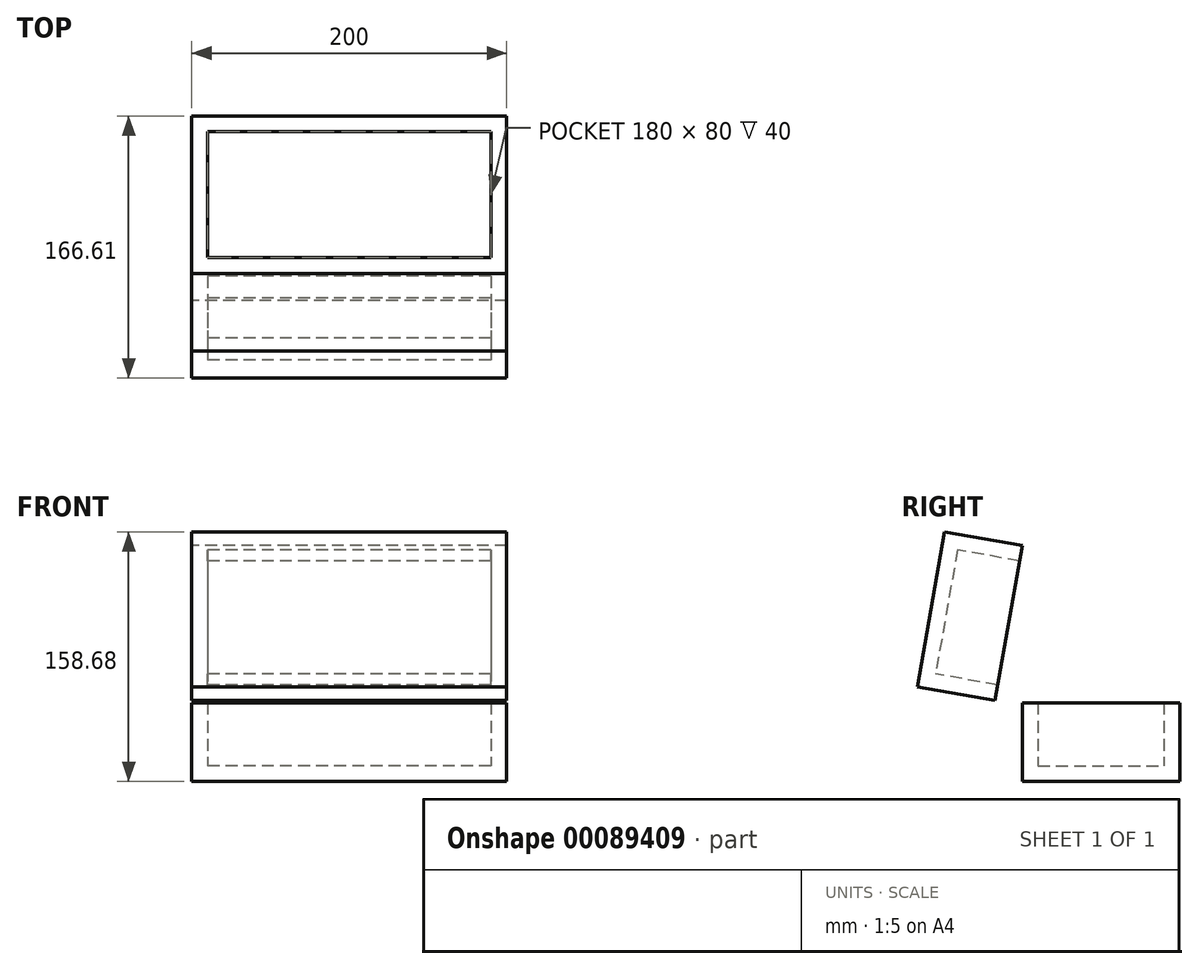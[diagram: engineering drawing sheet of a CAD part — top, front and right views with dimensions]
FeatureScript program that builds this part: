
annotation { "Feature Type Name" : "Feature", "Feature Type Description" : "" }
export const myFeature = defineFeature(function(context is Context, id is Id, definition is map)
    precondition{}
    {
        {
            var Q0;
            Q0=qCreatedBy(makeId("Top.planeOp"),FACE);
            var sketch = newSketch(context, id + "F0", { "sketchPlane" : qUnion([Q0])});
            skLineSegment(sketch, "E0.bottom", {"start": v(100, -50) * mm, "end": v(-100, -50) * mm});
            skLineSegment(sketch, "E0.top", {"start": v(100, 50) * mm, "end": v(-100, 50) * mm});
            skLineSegment(sketch, "E0.left", {"start": v(100, -50) * mm, "end": v(100, 50) * mm});
            skLineSegment(sketch, "E0.right", {"start": v(-100, -50) * mm, "end": v(-100, 50) * mm});
            skPoint(sketch, "E0.middle", {"position": v(0, 0) * mm});
            skSolve(sketch);
        }
        {
            var Q0;
            Q0 = qSketchRegion(id + "F0", true);
            extrude(context, id + "F1", {"entities" : qUnion([Q0]), "depth" : 50 * mm});
        }
        {
            var Q0;
            Q0=makeQuery(id+"F1.opExtrude","CAP_FACE",FACE,{"disambiguationData":[OSD([sQuery(id+"F0.wireOp",EDGE,"E0.bottom"),sQuery(id+"F0.wireOp",EDGE,"E0.top"),sQuery(id+"F0.wireOp",EDGE,"E0.left"),sQuery(id+"F0.wireOp",EDGE,"E0.right")])],"isStart":false});
            shell(context, id + "F2", {"entities" : qUnion([Q0]), "thickness" : 10 * mm});
        }
        {
            var Q0;
            Q0=makeQuery(id+"F1.opExtrude","SWEPT_BODY",BODY,{"disambiguationData":[OSD([sQuery(id+"F0.wireOp",EDGE,"E0.bottom"),sQuery(id+"F0.wireOp",EDGE,"E0.top"),sQuery(id+"F0.wireOp",EDGE,"E0.left"),sQuery(id+"F0.wireOp",EDGE,"E0.right")])]});
            transform(context, id + "F3", {"entities" : qUnion([Q0]), "transformType" : TransformType.TRANSLATION_3D, "dx" : 0 * mm, "dy" : 0 * mm, "dz" : 100 * mm, "makeCopy" : true});
        }
        {
            var Q0;
            Q0=makeQuery(id+"F3.opPattern","COPY",BODY,{"derivedFrom":makeQuery(id+"F1.opExtrude","SWEPT_BODY",BODY,{"disambiguationData":[OSD([sQuery(id+"F0.wireOp",EDGE,"E0.bottom"),sQuery(id+"F0.wireOp",EDGE,"E0.top"),sQuery(id+"F0.wireOp",EDGE,"E0.left"),sQuery(id+"F0.wireOp",EDGE,"E0.right")])]}),"instanceName":"1"});
            var Q1;
            Q1=makeQuery(id+"F3.opPattern","COPY",EDGE,{"derivedFrom":makeQuery(id+"F1.opExtrude","CAP_EDGE",EDGE,{"disambiguationData":[OSD([sQuery(id+"F0.wireOp",EDGE,"E0.bottom")])],"isStart":false}),"instanceName":"1"});
            transform(context, id + "F4", {"entities" : qUnion([Q0]), "transformType" : TransformType.ROTATION, "transformAxis" : qUnion([Q1]), "angle" : 100 * degree, "makeCopy" : false});
        }
    });
